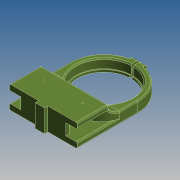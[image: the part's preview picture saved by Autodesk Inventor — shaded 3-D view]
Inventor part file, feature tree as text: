
AUTODESK INVENTOR PART (.ipt)
format: ipt  version: 2019 (Build 230136000, 136)  size: 680,448 bytes
history: native  units: mm
features: sketch x15, fillet x10, extrude x9, hole x6, projected_geometry x6, mirror x4, other x2, chamfer x1
ambient origin geometry x8: Origin, YZ Plane, XZ Plane, XY Plane, X Axis, Y Axis, Z Axis, Center Point
bodies: Solid2 (feature_tree)
feature tree (53):
  extrude  "Extrusion2"  Depth=20.0mm
  extrude  "Extrusion3"  Depth=10.0mm TaperAngle=0.0deg
  hole  "Trou pour ressort"  [1 undecoded]
  mirror  "Mirror1"
  extrude  "Extrusion5"  Depth=30.0mm
  extrude  "Extrusion6"  Depth=2.0mm TaperAngle=0.0deg
  hole  "Hole4"  [1 undecoded]
  fillet  "Fillet3"  Radius=60.0mm
  fillet  "Fillet4"  Radius=30.0mm
  hole  "Hole5"  [1 undecoded]
  extrude  "Extrusion12"  Depth=2.0mm
  extrude  "Extrusion13"  TaperAngle=0.0deg  [1 undecoded]
  fillet  "Fillet15"  Radius=1.0mm
  hole  "Hole9"  [1 undecoded]
  extrude  "Extrusion14"  Depth=1.0mm
  mirror  "Mirror3"
  other  "Work Axis1"
  hole  "Hole10"  [1 undecoded]
  fillet  "Fillet16"  Radius=1.0mm
  fillet  "Fillet17"  Radius=1.0mm
  fillet  "Fillet18"  Radius=3.0mm
  chamfer  "Chamfer2"  Distance=5.5mm
  fillet  "Fillet19"  Radius=3.0mm
  fillet  "Fillet22"  Radius=28.0mm
  fillet  "Fillet23"  Radius=4.0mm
  fillet  "Fillet24"  Radius=10.0mm
  extrude  "Extrusion16"  Depth=5.0mm
  other  "Work Axis2"
  hole  "Hole12"  [1 undecoded]
  mirror  "Mirror4"
  extrude  "Extrusion17"  Depth=20.0mm
  mirror  "Mirror5"
  sketch  "Sketch1"  dims[d14=20.0mm d15=20.0mm d16=0.0mm d19=3.0mm]
  sketch  "Sketch3"  dims[d20=5.0mm d21=10.0mm d22=0.0mm]
  sketch  "Sketch6"  dims[d42=22.0mm d43=4.1mm]
  sketch  "Sketch8"  dims[d44=30.0mm d45=3.0mm]
  sketch  "Sketch9"  dims[d49=4.0mm]
  sketch  "Sketch10"  dims[d50=5.0mm d51=6.0mm d52=4.0mm d53=2.0mm d54=90.0deg d55=8.0mm d56=20.594885mm d60=2.0mm d61=0.0mm]
  sketch  "Sketch12"  dims[d62=3.0mm d66=16.0mm d67=60.0mm d68=0.0mm d69=30.0mm]
  sketch  "Sketch21"  dims[d70=48.0mm d71=6.0mm d72=50.0mm d73=18.0mm d74=90.0deg d75=8.0mm d76=20.594885mm d77=30.0mm]
  sketch  "Sketch22"  dims[d78=11.5mm]
  sketch  "Sketch23"  dims[d79=6.0mm d80=6.0mm d81=4.0mm d82=2.0mm d83=90.0deg d84=8.0mm d85=20.594885mm d141=35.0mm]
  sketch  "Sketch24"  dims[d142=2.0mm d143=0.0mm d144=0.0mm d145=1.0mm]
  sketch  "Sketch25"  dims[d146=10.0mm d147=10.0mm d148=0.0mm]
  sketch  "Sketch28"  dims[d149=10.0mm]
  sketch  "Sketch29"  dims[d150=52.0mm d151=6.0mm d152=4.0mm d153=2.0mm d154=90.0deg d155=10.0mm d156=0.0mm d157=1.0mm]
  projected_geometry  "Projected Loop2"
  sketch  "Sketch30"  dims[d158=1.0mm d159=1.0mm d160=1.0mm d161=2.0mm d162=45.0deg d163=1.0mm d164=3.0mm d165=5.5mm d166=3.0mm d167=28.0mm d170=4.0mm d171=10.0mm d172=0.0mm d173=5.0mm d174=28.0mm d175=3.3mm d176=6.0mm d177=6.0mm d178=24.0mm d179=90.0deg d180=10.0mm d181=0.0mm d196=6.0mm d199=1.0mm d200=1.0mm d201=2.0mm d202=5.5mm d203=10.0mm d204=0.0mm d205=3.0mm d206=1.5mm d207=6.0mm d208=4.0mm d209=2.0mm d210=90.0deg d211=2.0mm d212=20.594885mm d213=6.0mm d214=3.0mm d215=2.5mm d216=5.0mm d217=83.0mm d218=0.0mm d219=20.0mm d220=17.0mm]
  projected_geometry  "Project Cut Edges2"
  projected_geometry  "Project Cut Edges4"
  projected_geometry  "Project Cut Edges5"
  projected_geometry  "Project Cut Edges7"
  projected_geometry  "Project Cut Edges8"
note: 7 required parameter values undecoded (feature->parameter linkage not recoverable at this tier; creation-order binding heuristic only, values carry confidence <= 0.55)
